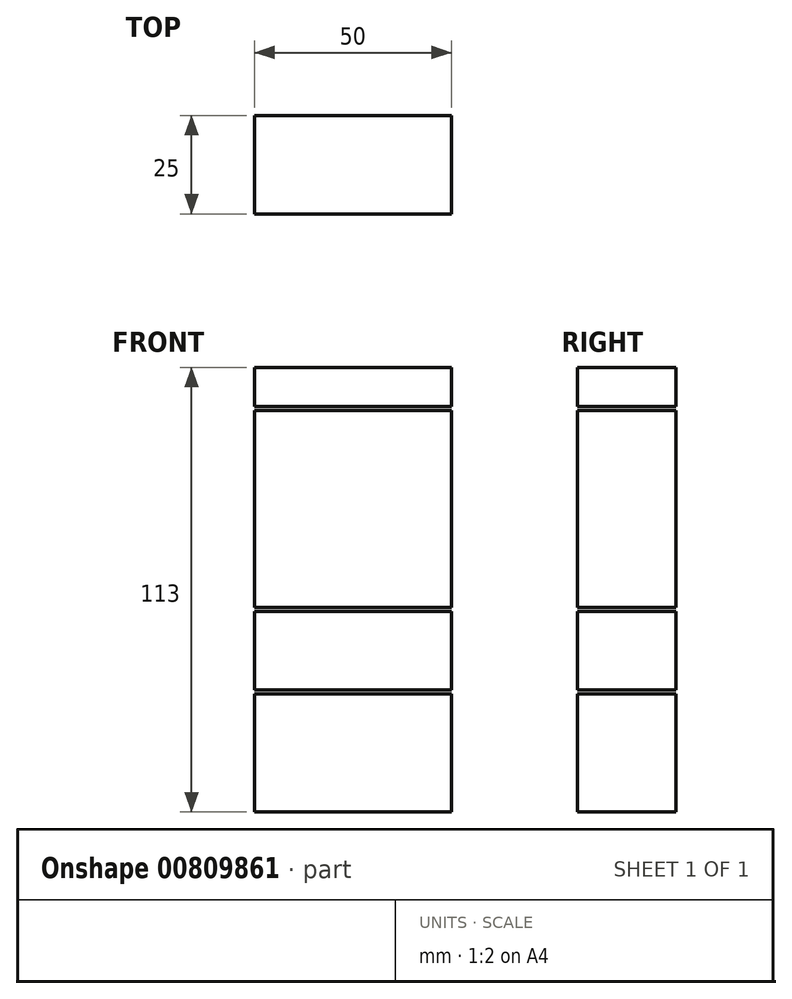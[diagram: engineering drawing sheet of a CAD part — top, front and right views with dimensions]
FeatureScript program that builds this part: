
annotation { "Feature Type Name" : "Feature", "Feature Type Description" : "" }
export const myFeature = defineFeature(function(context is Context, id is Id, definition is map)
    precondition{}
    {
        {
            var Q0;
            Q0=qCreatedBy(makeId("Front.planeOp"),FACE);
            var sketch = newSketch(context, id + "F0", { "sketchPlane" : qUnion([Q0])});
            skLineSegment(sketch, "E0.bottom", {"start": v(0, 0) * mm, "end": v(50, 0) * mm});
            skLineSegment(sketch, "E0.top", {"start": v(0, 30) * mm, "end": v(50, 30) * mm});
            skLineSegment(sketch, "E0.left", {"start": v(0, 0) * mm, "end": v(0, 30) * mm});
            skLineSegment(sketch, "E0.right", {"start": v(50, 0) * mm, "end": v(50, 30) * mm});
            skLineSegment(sketch, "E1.bottom", {"start": v(0, 31) * mm, "end": v(50, 31) * mm});
            skLineSegment(sketch, "E1.top", {"start": v(0, 51) * mm, "end": v(50, 51) * mm});
            skLineSegment(sketch, "E1.left", {"start": v(0, 31) * mm, "end": v(0, 51) * mm});
            skLineSegment(sketch, "E1.right", {"start": v(50, 31) * mm, "end": v(50, 51) * mm});
            skLineSegment(sketch, "E2.bottom", {"start": v(0, 52) * mm, "end": v(50, 52) * mm});
            skLineSegment(sketch, "E2.top", {"start": v(0, 102) * mm, "end": v(50, 102) * mm});
            skLineSegment(sketch, "E2.left", {"start": v(0, 52) * mm, "end": v(0, 102) * mm});
            skLineSegment(sketch, "E2.right", {"start": v(50, 52) * mm, "end": v(50, 102) * mm});
            skLineSegment(sketch, "E3.bottom", {"start": v(0, 103) * mm, "end": v(50, 103) * mm});
            skLineSegment(sketch, "E3.top", {"start": v(0, 113) * mm, "end": v(50, 113) * mm});
            skLineSegment(sketch, "E3.left", {"start": v(0, 103) * mm, "end": v(0, 113) * mm});
            skLineSegment(sketch, "E3.right", {"start": v(50, 103) * mm, "end": v(50, 113) * mm});
            skSolve(sketch);
        }
        {
            var Q0;
            Q0=qSketchRegion(id+"F0",true);
            extrude(context, id + "F1", {"entities" : qUnion([Q0]), "oppositeDirection" : true, "depth" : 25 * mm, "offsetDistance" : 25 * mm});
        }
    });
